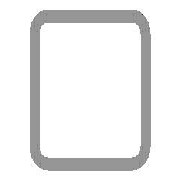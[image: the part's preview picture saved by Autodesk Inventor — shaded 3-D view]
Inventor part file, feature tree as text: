
AUTODESK INVENTOR PART (.ipt)
format: ipt  version: 2025.3 (Build 293356030, 356C)  size: 145,920 bytes
history: native  units: mm (DEFAULTED — no unit token found)
features: other x4, plane x3, split x2, sketch x1
ambient origin geometry x8: Origin, YZ Plane, XZ Plane, XY Plane, X Axis, Y Axis, Z Axis, Center Point
bodies: Solid1 (feature_tree), Body (feature_tree)
feature tree (10):
  parser-record x1  (decoder bookkeeping rows leaked as tree rows — omitted from the tree; the rows remain in map.json)
  other  "Driven Length"
  other  "Start Plane"
  other  "End Plane"
  plane  "Work Plane4"
  split  "Split1"
  plane  "Work Plane5"
  split  "Split2"
  sketch  "Sketch3"  dims[d3=2366.612931mm d4=0.0mm d7=6.0mm d9=80.0mm d11=80.0mm d12=3.0mm d13=153.387069mm d14=2520.0mm d15=40.0mm d16=40.0mm d17=90.0deg d18=2366.612931mm]
  plane  "Work Plane3"
